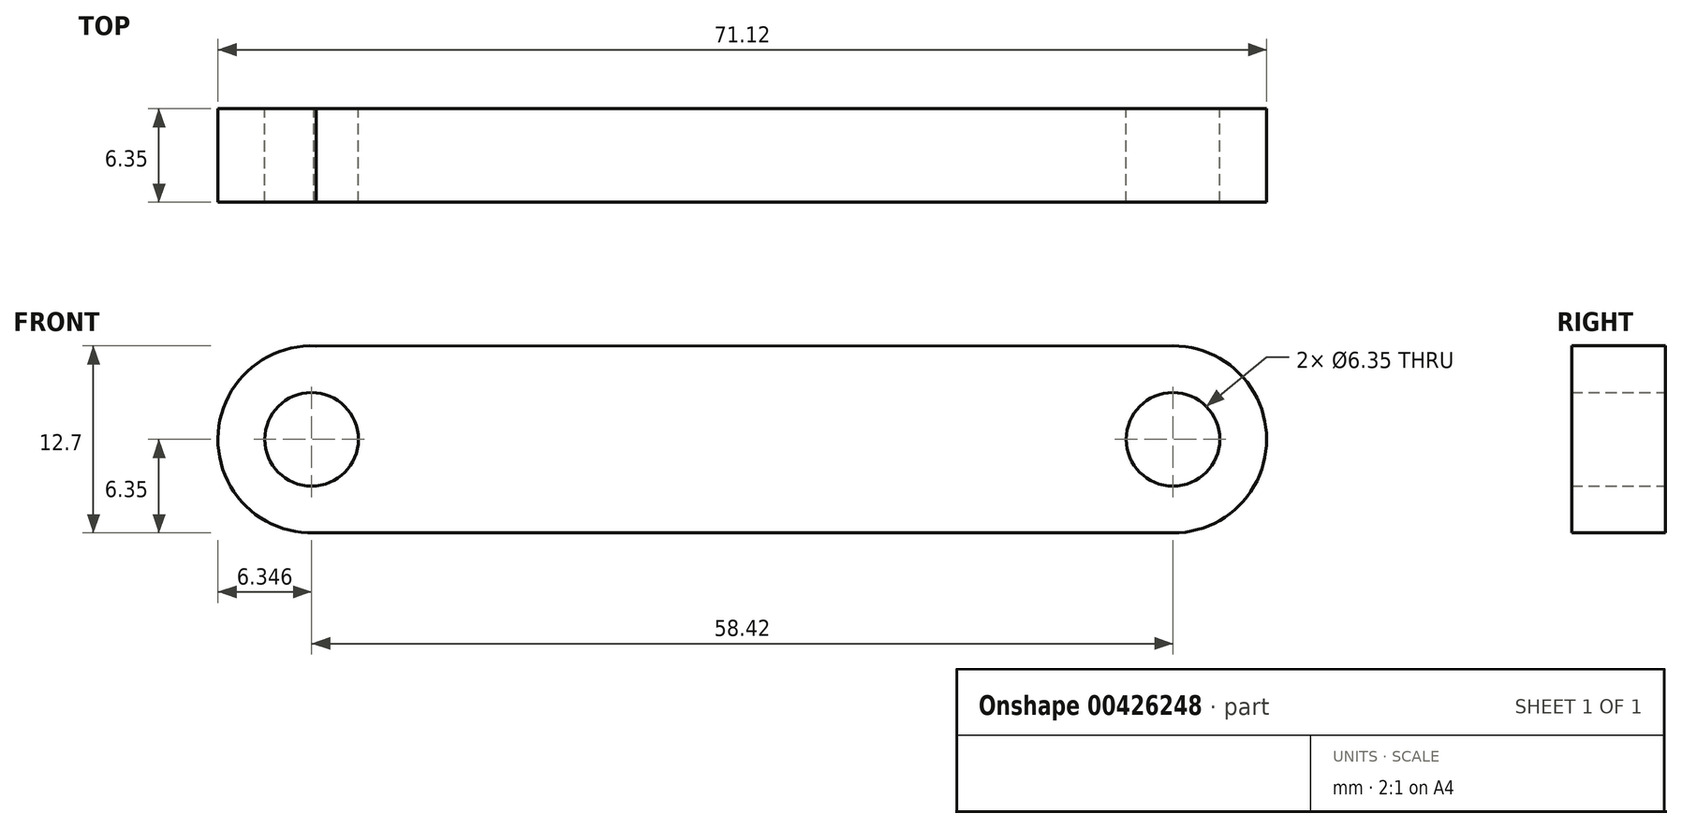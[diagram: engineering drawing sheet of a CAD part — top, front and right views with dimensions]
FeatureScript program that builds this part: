
annotation { "Feature Type Name" : "Feature", "Feature Type Description" : "" }
export const myFeature = defineFeature(function(context is Context, id is Id, definition is map)
    precondition{}
    {
        {
            var Q0;
            Q0=qCreatedBy(makeId("Front.planeOp"),FACE);
            var sketch = newSketch(context, id + "F0", { "sketchPlane" : qUnion([Q0])});
            skCircle(sketch, "E0", {"center": v(-69.62, 0) * mm, "radius": 6.35 * mm});
            skCircle(sketch, "E1", {"center": v(-69.62, 0) * mm, "radius": 3.18 * mm});
            skCircle(sketch, "E2", {"center": v(-11.2, 0) * mm, "radius": 6.35 * mm});
            skCircle(sketch, "E3", {"center": v(-11.2, 0) * mm, "radius": 3.18 * mm});
            skLineSegment(sketch, "E4", {"start": v(-69.92, 6.34) * mm, "end": v(-11.2, 6.35) * mm});
            skLineSegment(sketch, "E5", {"start": v(-69.8, -6.35) * mm, "end": v(-11.2, -6.35) * mm});
            skSolve(sketch);
        }
        {
            var Q0;
            Q0 = qSketchRegion(id + "F0", true);
            extrude(context, id + "F1", {"entities" : qUnion([Q0]), "depth" : 6.35 * mm});
        }
    });
